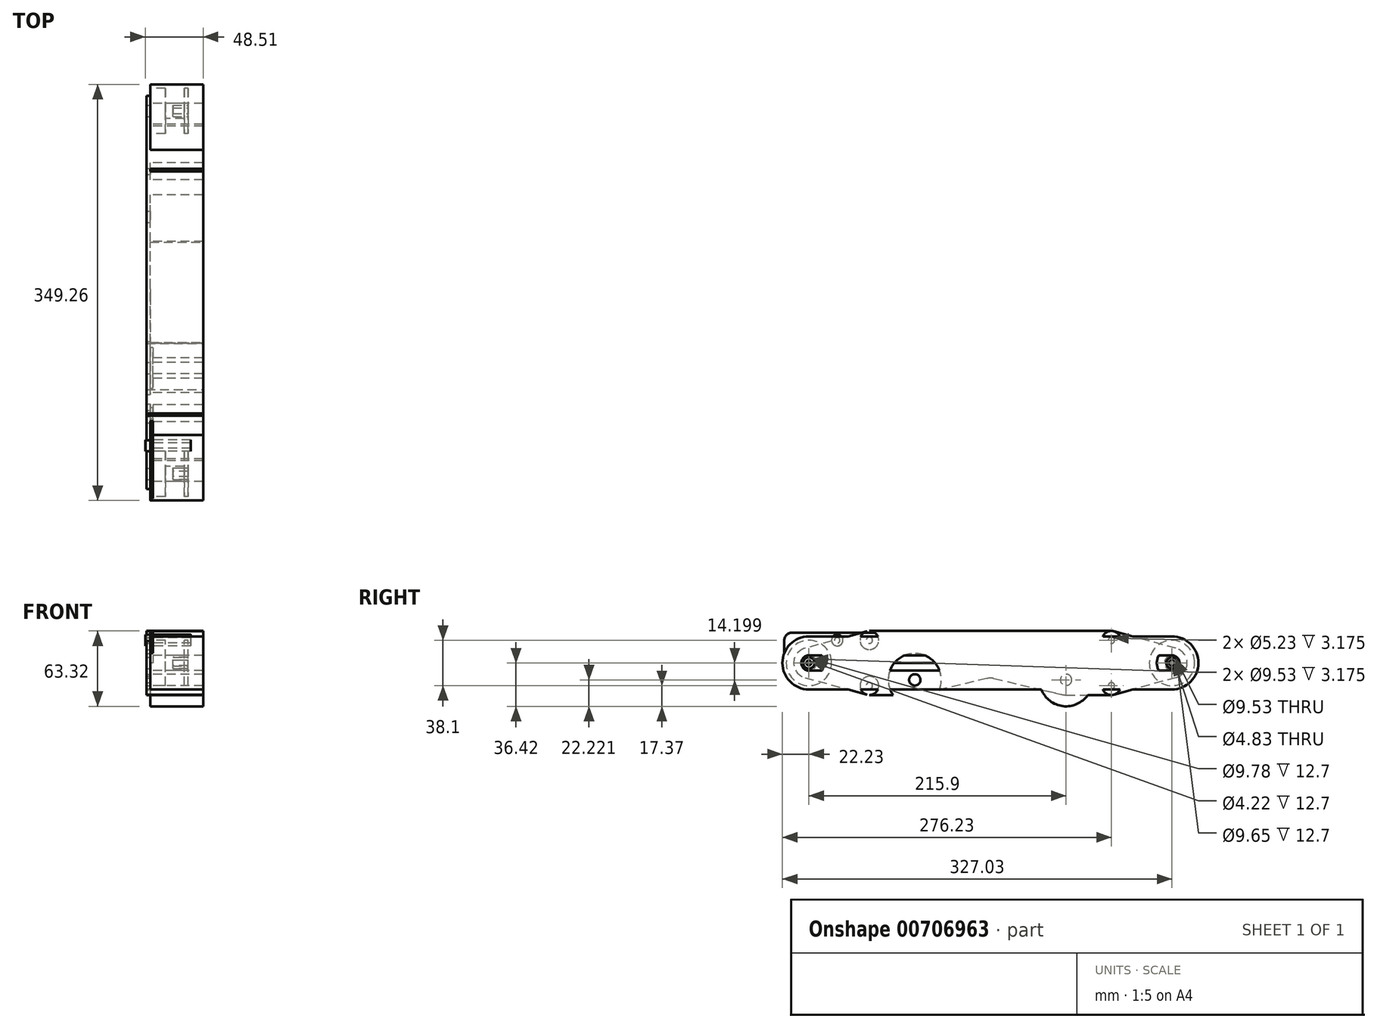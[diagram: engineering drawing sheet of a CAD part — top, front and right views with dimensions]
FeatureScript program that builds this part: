
annotation { "Feature Type Name" : "Feature", "Feature Type Description" : "" }
export const myFeature = defineFeature(function(context is Context, id is Id, definition is map)
    precondition{}
    {
        {
            var Q0;
            Q0=qCreatedBy(makeId("Right.planeOp"),FACE);
            var sketch = newSketch(context, id + "F0", { "sketchPlane" : qUnion([Q0])});
            skCircle(sketch, "E0", {"center": v(0, 0) * mm, "radius": 19.05 * mm});
            skCircle(sketch, "E1", {"center": v(304.8, 0) * mm, "radius": 19.05 * mm});
            skCircle(sketch, "E2", {"center": v(0, 0) * mm, "radius": 6.35 * mm});
            skCircle(sketch, "E3", {"center": v(304.8, 0) * mm, "radius": 6.35 * mm});
            skSolve(sketch);
        }
        {
            var Q0;
            Q0=makeQuery(id+"F0.imprint","IMPRINT",FACE,{"disambiguationData":[TD([[makeQuery(id+"F0.imprint","IMPRINT",EDGE,{"derivedFrom":sQuery(id+"F0.wireOp",EDGE,"E0")}),1.0]])]});
            var Q1;
            Q1=makeQuery(id+"F0.imprint","IMPRINT",FACE,{"disambiguationData":[TD([[makeQuery(id+"F0.imprint","IMPRINT",EDGE,{"derivedFrom":sQuery(id+"F0.wireOp",EDGE,"E1")}),1.0]])]});
            var Q2;
            Q2=makeQuery(id+"F0.imprint","IMPRINT",FACE,{"disambiguationData":[TD([[makeQuery(id+"F0.imprint","IMPRINT",EDGE,{"derivedFrom":sQuery(id+"F0.wireOp",EDGE,"E2")}),1.0]])]});
            var Q3;
            Q3=makeQuery(id+"F0.imprint","IMPRINT",FACE,{"disambiguationData":[TD([[makeQuery(id+"F0.imprint","IMPRINT",EDGE,{"derivedFrom":sQuery(id+"F0.wireOp",EDGE,"E3")}),1.0]])]});
            extrude(context, id + "F1", {"entities" : qUnion([Q0, Q1, Q2, Q3]), "depth" : 31.75 * mm, "offsetDistance" : 25.4 * mm});
        }
        {
            var Q0;
            Q0 = qSketchRegion(id + "F0", true);
            extrude(context, id + "F2", {"entities" : qUnion([Q0]), "operationType" : NewBodyOperationType.REMOVE, "depth" : 28.57 * mm, "offsetDistance" : 25.4 * mm, "hasSecondDirection" : true, "secondDirectionOppositeDirection" : true, "secondDirectionDepth" : -12.7 * mm});
        }
        {
            var Q0;
            Q0=qCreatedBy(makeId("Right.planeOp"),FACE);
            var sketch = newSketch(context, id + "F3", { "sketchPlane" : qUnion([Q0])});
            skCircle(sketch, "E4", {"center": v(0, 0) * mm, "radius": 12.7 * mm});
            skCircle(sketch, "E5", {"center": v(304.8, 0) * mm, "radius": 12.7 * mm});
            skLineSegment(sketch, "E6.bottom", {"start": v(25.4, 25.4) * mm, "end": v(279.4, 25.4) * mm, "construction": true});
            skLineSegment(sketch, "E6.top", {"start": v(25.4, -25.4) * mm, "end": v(279.4, -25.4) * mm, "construction": true});
            skLineSegment(sketch, "E6.left", {"start": v(25.4, 25.4) * mm, "end": v(25.4, -25.4) * mm, "construction": true});
            skLineSegment(sketch, "E6.right", {"start": v(279.4, 25.4) * mm, "end": v(279.4, -25.4) * mm, "construction": true});
            skLineSegment(sketch, "E7", {"start": v(25.4, 25.4) * mm, "end": v(-5.23, 11.58) * mm, "construction": true});
            skLineSegment(sketch, "E8", {"start": v(25.4, -25.4) * mm, "end": v(-5.23, -11.58) * mm, "construction": true});
            skLineSegment(sketch, "E9", {"start": v(279.4, 25.4) * mm, "end": v(310.03, 11.58) * mm, "construction": true});
            skLineSegment(sketch, "E10", {"start": v(279.4, -25.4) * mm, "end": v(310.03, -11.58) * mm, "construction": true});
            skCircle(sketch, "E11", {"center": v(0, 0) * mm, "radius": 4.76 * mm});
            skCircle(sketch, "E12", {"center": v(304.8, 0) * mm, "radius": 4.76 * mm});
            skCircle(sketch, "E13", {"center": v(215.9, -14.2) * mm, "radius": 4.76 * mm});
            skCircle(sketch, "E14", {"center": v(215.9, -14.2) * mm, "radius": 22.23 * mm});
            skCircle(sketch, "E15.0", {"center": v(304.8, 0) * mm, "radius": 19.05 * mm, "construction": true});
            skCircle(sketch, "E16.0", {"center": v(0, 0) * mm, "radius": 19.05 * mm, "construction": true});
            skLineSegment(sketch, "E17", {"start": v(152.4, 25.4) * mm, "end": v(152.4, -25.4) * mm, "construction": true});
            skCircle(sketch, "E18.MirrorC", {"center": v(88.9, -14.2) * mm, "radius": 22.23 * mm});
            skCircle(sketch, "E19.MirrorC", {"center": v(88.9, -14.2) * mm, "radius": 4.76 * mm});
            skCircle(sketch, "E20", {"center": v(215.9, -14.2) * mm, "radius": 12.7 * mm});
            skCircle(sketch, "E21.MirrorC", {"center": v(88.9, -14.2) * mm, "radius": 12.7 * mm});
            skCircle(sketch, "E22", {"center": v(254, 19.05) * mm, "radius": 2.62 * mm});
            skCircle(sketch, "E23", {"center": v(254, -19.05) * mm, "radius": 2.62 * mm});
            skLineSegment(sketch, "E24", {"start": v(254, 19.05) * mm, "end": v(254, -19.05) * mm, "construction": true});
            skCircle(sketch, "E25.MirrorC", {"center": v(50.8, -19.05) * mm, "radius": 2.62 * mm});
            skCircle(sketch, "E26.MirrorC", {"center": v(50.8, 19.05) * mm, "radius": 2.62 * mm});
            skCircle(sketch, "E27", {"center": v(254, 19.05) * mm, "radius": 7.85 * mm});
            skCircle(sketch, "E28", {"center": v(254, -19.05) * mm, "radius": 7.85 * mm});
            skLineSegment(sketch, "E29", {"start": v(304.8, 0) * mm, "end": v(0, 0) * mm, "construction": true});
            skCircle(sketch, "E30.MirrorC", {"center": v(50.8, -19.05) * mm, "radius": 7.85 * mm});
            skCircle(sketch, "E31.MirrorC", {"center": v(50.8, 19.05) * mm, "radius": 7.85 * mm});
            skLineSegment(sketch, "E32", {"start": v(48.71, 26.62) * mm, "end": v(-3.38, 12.24) * mm});
            skLineSegment(sketch, "E33", {"start": v(254, 26.9) * mm, "end": v(50.8, 26.9) * mm});
            skLineSegment(sketch, "E34", {"start": v(308.18, 12.24) * mm, "end": v(256.09, 26.62) * mm});
            skLineSegment(sketch, "E35", {"start": v(308.18, -12.24) * mm, "end": v(256.09, -26.62) * mm});
            skLineSegment(sketch, "E36", {"start": v(215.9, -26.9) * mm, "end": v(254, -26.9) * mm});
            skLineSegment(sketch, "E37", {"start": v(88.9, -26.9) * mm, "end": v(50.8, -26.9) * mm});
            skLineSegment(sketch, "E38", {"start": v(-3.38, -12.24) * mm, "end": v(48.71, -26.62) * mm});
            skLineSegment(sketch, "E39", {"start": v(215.9, -14.2) * mm, "end": v(88.9, -14.2) * mm, "construction": true});
            skCircle(sketch, "E40", {"center": v(152.4, -25.4) * mm, "radius": 12.7 * mm, "construction": true});
            skLineSegment(sketch, "E41", {"start": v(155.3, -13.04) * mm, "end": v(213, -26.56) * mm});
            skLineSegment(sketch, "E42", {"start": v(149.5, -13.04) * mm, "end": v(91.8, -26.56) * mm});
            skArc(sketch, "E43", {"start": v(155.3, -13.04) * mm, "mid": v(152.4, -12.7) * mm, "end": v(149.5, -13.04) * mm});
            skSolve(sketch);
        }
        {
            var Q0;
            Q0=makeQuery(id+"F3.imprint","IMPRINT",FACE,{"disambiguationData":[TD([[makeQuery(id+"F3.imprint","IMPRINT",EDGE,{"derivedFrom":sQuery(id+"F3.wireOp",EDGE,"E11")}),-1.0]])]});
            var Q1;
            Q1=makeQuery(id+"F3.imprint","IMPRINT",FACE,{"disambiguationData":[TD([[makeQuery(id+"F3.imprint","IMPRINT",EDGE,{"derivedFrom":sQuery(id+"F3.wireOp",EDGE,"E6.left")}),-1.0]])]});
            var Q2;
            Q2=makeQuery(id+"F3.imprint","IMPRINT",FACE,{"disambiguationData":[TD([[makeQuery(id+"F3.imprint","IMPRINT",EDGE,{"derivedFrom":sQuery(id+"F3.wireOp",EDGE,"E6.bottom")}),-1.0]])]});
            var Q3;
            Q3=makeQuery(id+"F3.imprint","IMPRINT",FACE,{"disambiguationData":[TD([[makeQuery(id+"F3.imprint","IMPRINT",EDGE,{"derivedFrom":sQuery(id+"F3.wireOp",EDGE,"E12")}),-1.0]])]});
            var Q4;
            Q4=makeQuery(id+"F3.imprint","IMPRINT",FACE,{"disambiguationData":[TD([[makeQuery(id+"F3.imprint","IMPRINT",EDGE,{"derivedFrom":sQuery(id+"F3.wireOp",EDGE,"E6.right")}),1.0]])]});
            var Q5;
            {var subQ1=sQuery(id+"F3.wireOp",EDGE,"E32");Q5=makeQuery(id+"F3.imprint","IMPRINT",FACE,{"disambiguationData":[TD([[makeQuery(id+"F3.imprint","IMPRINT",EDGE,{"derivedFrom":subQ1}),1.0]])]});}
            var Q6;
            Q6=makeQuery(id+"F3.imprint","IMPRINT",FACE,{"disambiguationData":[TD([[makeQuery(id+"F3.imprint","IMPRINT",EDGE,{"derivedFrom":sQuery(id+"F3.wireOp",EDGE,"E26.MirrorC")}),1.0]])]});
            var Q7;
            Q7=makeQuery(id+"F3.imprint","IMPRINT",FACE,{"disambiguationData":[TD([[makeQuery(id+"F3.imprint","IMPRINT",EDGE,{"derivedFrom":sQuery(id+"F3.wireOp",EDGE,"E25.MirrorC")}),1.0]])]});
            var Q8;
            Q8=makeQuery(id+"F3.imprint","IMPRINT",FACE,{"disambiguationData":[TD([[makeQuery(id+"F3.imprint","IMPRINT",EDGE,{"derivedFrom":sQuery(id+"F3.wireOp",EDGE,"E19.MirrorC")}),1.0]])]});
            var Q9;
            {var subQ0=sQuery(id+"F3.wireOp",EDGE,"E37");var subQ1=sQuery(id+"F3.wireOp",EDGE,"E18.MirrorC");var subQ2=makeQuery(id+"F3.imprint","INTERSECT",VERTEX,{"derivedFrom":[subQ1,subQ0]});Q9=makeQuery(id+"F3.imprint","IMPRINT",FACE,{"disambiguationData":[TD([[makeQuery(id+"F3.imprint","IMPRINT",EDGE,{"disambiguationData":[TD([[subQ2,-1.0]])],"derivedFrom":subQ1}),-1.0]])]});}
            var Q10;
            Q10=makeQuery(id+"F3.imprint","IMPRINT",FACE,{"disambiguationData":[TD([[makeQuery(id+"F3.imprint","IMPRINT",EDGE,{"derivedFrom":sQuery(id+"F3.wireOp",EDGE,"E23")}),-1.0]])]});
            var Q11;
            Q11=makeQuery(id+"F3.imprint","IMPRINT",FACE,{"disambiguationData":[TD([[makeQuery(id+"F3.imprint","IMPRINT",EDGE,{"derivedFrom":sQuery(id+"F3.wireOp",EDGE,"E22")}),-1.0]])]});
            var Q12;
            Q12=makeQuery(id+"F3.imprint","IMPRINT",FACE,{"disambiguationData":[TD([[makeQuery(id+"F3.imprint","IMPRINT",EDGE,{"derivedFrom":sQuery(id+"F3.wireOp",EDGE,"E13")}),-1.0]])]});
            var Q13;
            {var subQ0=sQuery(id+"F3.wireOp",EDGE,"E36");var subQ1=sQuery(id+"F3.wireOp",EDGE,"E14");var subQ2=makeQuery(id+"F3.imprint","INTERSECT",VERTEX,{"derivedFrom":[subQ1,subQ0]});Q13=makeQuery(id+"F3.imprint","IMPRINT",FACE,{"disambiguationData":[TD([[makeQuery(id+"F3.imprint","IMPRINT",EDGE,{"disambiguationData":[TD([[subQ2,-1.0]])],"derivedFrom":subQ1}),1.0]])]});}
            extrude(context, id + "F4", {"entities" : qUnion([Q0, Q1, Q2, Q3, Q4, Q5, Q6, Q7, Q8, Q9, Q10, Q11, Q12, Q13]), "oppositeDirection" : true, "depth" : 3.17 * mm, "offsetDistance" : 25.4 * mm});
        }
        {
            var Q0;
            {var subQ0=sQuery(id+"F3.wireOp",EDGE,"E37");var subQ1=sQuery(id+"F3.wireOp",EDGE,"E18.MirrorC");var subQ2=makeQuery(id+"F3.imprint","INTERSECT",VERTEX,{"derivedFrom":[subQ1,subQ0]});Q0=makeQuery(id+"F3.imprint","IMPRINT",FACE,{"disambiguationData":[TD([[makeQuery(id+"F3.imprint","IMPRINT",EDGE,{"disambiguationData":[TD([[subQ2,1.0]])],"derivedFrom":subQ1}),-1.0]])]});}
            var Q1;
            {var subQ0=sQuery(id+"F3.wireOp",EDGE,"E37");var subQ1=sQuery(id+"F3.wireOp",EDGE,"E18.MirrorC");var subQ2=makeQuery(id+"F3.imprint","INTERSECT",VERTEX,{"derivedFrom":[subQ1,subQ0]});Q1=makeQuery(id+"F3.imprint","IMPRINT",FACE,{"disambiguationData":[TD([[makeQuery(id+"F3.imprint","IMPRINT",EDGE,{"disambiguationData":[TD([[subQ2,-1.0]])],"derivedFrom":subQ1}),-1.0]])]});}
            var Q2;
            Q2=makeQuery(id+"F3.imprint","IMPRINT",FACE,{"disambiguationData":[TD([[makeQuery(id+"F3.imprint","IMPRINT",EDGE,{"derivedFrom":sQuery(id+"F3.wireOp",EDGE,"E19.MirrorC")}),1.0]])]});
            var Q3;
            {var subQ0=sQuery(id+"F3.wireOp",EDGE,"E36");var subQ1=sQuery(id+"F3.wireOp",EDGE,"E14");var subQ2=makeQuery(id+"F3.imprint","INTERSECT",VERTEX,{"derivedFrom":[subQ1,subQ0]});Q3=makeQuery(id+"F3.imprint","IMPRINT",FACE,{"disambiguationData":[TD([[makeQuery(id+"F3.imprint","IMPRINT",EDGE,{"disambiguationData":[TD([[subQ2,-1.0]])],"derivedFrom":subQ1}),1.0]])]});}
            var Q4;
            Q4=makeQuery(id+"F3.imprint","IMPRINT",FACE,{"disambiguationData":[TD([[makeQuery(id+"F3.imprint","IMPRINT",EDGE,{"derivedFrom":sQuery(id+"F3.wireOp",EDGE,"E13")}),-1.0]])]});
            var Q5;
            {var subQ0=sQuery(id+"F3.wireOp",EDGE,"E36");var subQ1=sQuery(id+"F3.wireOp",EDGE,"E14");var subQ2=makeQuery(id+"F3.imprint","INTERSECT",VERTEX,{"derivedFrom":[subQ1,subQ0]});Q5=makeQuery(id+"F3.imprint","IMPRINT",FACE,{"disambiguationData":[TD([[makeQuery(id+"F3.imprint","IMPRINT",EDGE,{"disambiguationData":[TD([[subQ2,1.0]])],"derivedFrom":subQ1}),1.0]])]});}
            extrude(context, id + "F5", {"entities" : qUnion([Q0, Q1, Q2, Q3, Q4, Q5]), "depth" : 44.45 * mm, "offsetDistance" : 25.4 * mm});
        }
        {
            var Q0;
            Q0=qCreatedBy(makeId("Right.planeOp"),FACE);
            var sketch = newSketch(context, id + "F6", { "sketchPlane" : qUnion([Q0])});
            skCircle(sketch, "E44.0", {"center": v(0, 0) * mm, "radius": 6.35 * mm});
            skCircle(sketch, "E45.0", {"center": v(304.8, 0) * mm, "radius": 6.35 * mm});
            skCircle(sketch, "E46", {"center": v(0, 0) * mm, "radius": 22.23 * mm});
            skCircle(sketch, "E47.0", {"center": v(0, 0) * mm, "radius": 19.05 * mm, "construction": true});
            skCircle(sketch, "E48.0", {"center": v(304.8, 0) * mm, "radius": 19.05 * mm, "construction": true});
            skCircle(sketch, "E49", {"center": v(304.8, 0) * mm, "radius": 22.23 * mm});
            skLineSegment(sketch, "E50", {"start": v(0, 6.35) * mm, "end": v(304.8, 6.35) * mm});
            skLineSegment(sketch, "E51", {"start": v(304.8, 22.23) * mm, "end": v(0, 22.23) * mm});
            skLineSegment(sketch, "E52", {"start": v(0, -6.35) * mm, "end": v(304.8, -6.35) * mm});
            skLineSegment(sketch, "E53", {"start": v(0, -22.23) * mm, "end": v(304.8, -22.22) * mm});
            skSolve(sketch);
        }
        {
            var Q0;
            {var subQ0=sQuery(id+"F6.wireOp",EDGE,"E51");Q0=makeQuery(id+"F6.imprint","IMPRINT",FACE,{"disambiguationData":[TD([[makeQuery(id+"F6.imprint","IMPRINT",EDGE,{"derivedFrom":subQ0}),1.0]])]});}
            var Q1;
            {var subQ5=sQuery(id+"F6.wireOp",EDGE,"E50");var subQ7=sQuery(id+"F6.wireOp",EDGE,"E44.0");var subQ9=makeQuery(id+"F6.imprint","INTERSECT",VERTEX,{"derivedFrom":[subQ7,subQ5]});Q1=makeQuery(id+"F6.imprint","IMPRINT",FACE,{"disambiguationData":[TD([[makeQuery(id+"F6.imprint","IMPRINT",EDGE,{"disambiguationData":[TD([[subQ9,-1.0]])],"derivedFrom":subQ7}),-1.0]])]});}
            var Q2;
            {var subQ0=sQuery(id+"F6.wireOp",EDGE,"E53");Q2=makeQuery(id+"F6.imprint","IMPRINT",FACE,{"disambiguationData":[TD([[makeQuery(id+"F6.imprint","IMPRINT",EDGE,{"derivedFrom":subQ0}),1.0]])]});}
            var Q3;
            {var subQ5=sQuery(id+"F6.wireOp",EDGE,"E50");var subQ7=sQuery(id+"F6.wireOp",EDGE,"E45.0");var subQ8=makeQuery(id+"F6.imprint","INTERSECT",VERTEX,{"derivedFrom":[subQ7,subQ5]});Q3=makeQuery(id+"F6.imprint","IMPRINT",FACE,{"disambiguationData":[TD([[makeQuery(id+"F6.imprint","IMPRINT",EDGE,{"disambiguationData":[TD([[subQ8,1.0]])],"derivedFrom":subQ7}),-1.0]])]});}
            extrude(context, id + "F7", {"entities" : qUnion([Q0, Q1, Q2, Q3]), "depth" : 44.45 * mm, "offsetDistance" : 25.4 * mm});
        }
        {
            var Q0;
            Q0=qCreatedBy(makeId("Right.planeOp"),FACE);
            var sketch = newSketch(context, id + "F8", { "sketchPlane" : qUnion([Q0])});
            skLineSegment(sketch, "E54.bottom", {"start": v(-14.29, 25.4) * mm, "end": v(227.01, 25.4) * mm});
            skLineSegment(sketch, "E54.top", {"start": v(-14.29, 0) * mm, "end": v(227.01, 0) * mm});
            skLineSegment(sketch, "E54.left", {"start": v(-20.64, 19.05) * mm, "end": v(-20.64, 6.35) * mm});
            skLineSegment(sketch, "E54.right", {"start": v(233.36, 19.05) * mm, "end": v(233.36, 6.35) * mm});
            skPoint(sketch, "E55.visualSharp", {"position": v(-20.64, 25.4) * mm});
            skArc(sketch, "E55.filletArc", {"start": v(-14.29, 25.4) * mm, "mid": v(-18.78, 23.54) * mm, "end": v(-20.64, 19.05) * mm});
            skPoint(sketch, "E56.visualSharp", {"position": v(-20.64, 0) * mm});
            skArc(sketch, "E56.filletArc", {"start": v(-20.64, 6.35) * mm, "mid": v(-18.78, 1.86) * mm, "end": v(-14.29, 0) * mm});
            skPoint(sketch, "E57.visualSharp", {"position": v(233.36, 0) * mm});
            skArc(sketch, "E57.filletArc", {"start": v(227.01, 0) * mm, "mid": v(231.5, 1.86) * mm, "end": v(233.36, 6.35) * mm});
            skPoint(sketch, "E58.visualSharp", {"position": v(233.36, 25.4) * mm});
            skArc(sketch, "E58.filletArc", {"start": v(233.36, 19.05) * mm, "mid": v(231.5, 23.54) * mm, "end": v(227.01, 25.4) * mm});
            skCircle(sketch, "E59", {"center": v(-7.94, 12.7) * mm, "radius": 4.76 * mm});
            skCircle(sketch, "E60", {"center": v(0, 12.7) * mm, "radius": 2.03 * mm});
            skCircle(sketch, "E61", {"center": v(-15.88, 12.7) * mm, "radius": 2.03 * mm});
            skLineSegment(sketch, "E62", {"start": v(-15.88, 12.7) * mm, "end": v(0, 12.7) * mm, "construction": true});
            skLineSegment(sketch, "E63", {"start": v(0, 12.7) * mm, "end": v(220.66, 12.7) * mm, "construction": true});
            skCircle(sketch, "E64", {"center": v(55.56, 12.7) * mm, "radius": 2.29 * mm});
            skCircle(sketch, "E65", {"center": v(157.16, 12.7) * mm, "radius": 2.29 * mm});
            skCircle(sketch, "E66", {"center": v(220.66, 12.7) * mm, "radius": 2.29 * mm});
            skCircle(sketch, "E67", {"center": v(23.81, 19.05) * mm, "radius": 2.29 * mm});
            skCircle(sketch, "E68", {"center": v(23.81, 6.35) * mm, "radius": 2.29 * mm});
            skCircle(sketch, "E69", {"center": v(188.91, 19.05) * mm, "radius": 2.29 * mm});
            skCircle(sketch, "E70", {"center": v(188.91, 6.35) * mm, "radius": 2.29 * mm});
            skLineSegment(sketch, "E71", {"start": v(23.81, 19.05) * mm, "end": v(188.91, 19.05) * mm, "construction": true});
            skLineSegment(sketch, "E72", {"start": v(188.91, 6.35) * mm, "end": v(23.81, 6.35) * mm, "construction": true});
            skLineSegment(sketch, "E73", {"start": v(106.36, 25.4) * mm, "end": v(106.36, 0) * mm, "construction": true});
            skLineSegment(sketch, "E74", {"start": v(188.91, 19.05) * mm, "end": v(188.91, 6.35) * mm, "construction": true});
            skLineSegment(sketch, "E75", {"start": v(23.81, 19.05) * mm, "end": v(23.81, 6.35) * mm, "construction": true});
            skCircle(sketch, "E76", {"center": v(106.36, 19.05) * mm, "radius": 2.29 * mm});
            skCircle(sketch, "E77", {"center": v(106.36, 6.35) * mm, "radius": 2.29 * mm});
            skSolve(sketch);
        }
        {
            var Q0;
            Q0=makeQuery(id+"F8.imprint","IMPRINT",FACE,{"disambiguationData":[TD([[makeQuery(id+"F8.imprint","IMPRINT",EDGE,{"derivedFrom":sQuery(id+"F8.wireOp",EDGE,"E54.bottom")}),-1.0]])]});
            extrude(context, id + "F9", {"entities" : qUnion([Q0]), "depth" : 2.3 * mm, "offsetDistance" : 25.4 * mm});
        }
        {
            var Q0;
            Q0=makeQuery(id+"F9.opExtrude","CAP_FACE",FACE,{"disambiguationData":[OSD([sQuery(id+"F8.wireOp",EDGE,"E54.bottom"),sQuery(id+"F8.wireOp",EDGE,"E54.top"),sQuery(id+"F8.wireOp",EDGE,"E54.left"),sQuery(id+"F8.wireOp",EDGE,"E54.right"),sQuery(id+"F8.wireOp",EDGE,"E55.filletArc"),sQuery(id+"F8.wireOp",EDGE,"E56.filletArc"),sQuery(id+"F8.wireOp",EDGE,"E57.filletArc"),sQuery(id+"F8.wireOp",EDGE,"E58.filletArc"),sQuery(id+"F8.wireOp",EDGE,"E59"),sQuery(id+"F8.wireOp",EDGE,"E60"),sQuery(id+"F8.wireOp",EDGE,"E61"),sQuery(id+"F8.wireOp",EDGE,"E64"),sQuery(id+"F8.wireOp",EDGE,"E65"),sQuery(id+"F8.wireOp",EDGE,"E66"),sQuery(id+"F8.wireOp",EDGE,"E67"),sQuery(id+"F8.wireOp",EDGE,"E68"),sQuery(id+"F8.wireOp",EDGE,"E69"),sQuery(id+"F8.wireOp",EDGE,"E70"),sQuery(id+"F8.wireOp",EDGE,"E76"),sQuery(id+"F8.wireOp",EDGE,"E77")])],"isStart":false});
            var sketch = newSketch(context, id + "F10", { "sketchPlane" : qUnion([Q0])});
            skCircle(sketch, "E78.0", {"center": v(23.81, 19.05) * mm, "radius": 2.29 * mm});
            skCircle(sketch, "E79", {"center": v(23.81, 19.05) * mm, "radius": 4.76 * mm});
            skCircle(sketch, "E80", {"center": v(23.81, 19.05) * mm, "radius": 2.03 * mm});
            skSolve(sketch);
        }
        {
            var Q0;
            Q0=makeQuery(id+"F10.imprint","IMPRINT",FACE,{"disambiguationData":[TD([[makeQuery(id+"F10.imprint","IMPRINT",EDGE,{"derivedFrom":sQuery(id+"F10.wireOp",EDGE,"E78.0")}),-1.0]])]});
            extrude(context, id + "F11", {"entities" : qUnion([Q0]), "depth" : 31.75 * mm, "offsetDistance" : 25.4 * mm});
        }
        {
            var Q0;
            Q0=makeQuery(id+"F10.imprint","IMPRINT",FACE,{"disambiguationData":[TD([[makeQuery(id+"F10.imprint","IMPRINT",EDGE,{"derivedFrom":sQuery(id+"F10.wireOp",EDGE,"E80")}),1.0]])]});
            extrude(context, id + "F12", {"entities" : qUnion([Q0]), "depth" : 38.1 * mm, "offsetDistance" : 25.4 * mm, "hasSecondDirection" : true, "secondDirectionOppositeDirection" : true, "secondDirectionDepth" : 2.3 * mm});
        }
        {
            var Q0;
            Q0=makeQuery(id+"F10.imprint","IMPRINT",FACE,{"disambiguationData":[TD([[makeQuery(id+"F10.imprint","IMPRINT",EDGE,{"derivedFrom":sQuery(id+"F10.wireOp",EDGE,"E78.0")}),-1.0]])]});
            var Q1;
            Q1=makeQuery(id+"F10.imprint","IMPRINT",FACE,{"disambiguationData":[TD([[makeQuery(id+"F10.imprint","IMPRINT",EDGE,{"derivedFrom":sQuery(id+"F10.wireOp",EDGE,"E78.0")}),1.0]])]});
            var Q2;
            Q2=makeQuery(id+"F10.imprint","IMPRINT",FACE,{"disambiguationData":[TD([[makeQuery(id+"F10.imprint","IMPRINT",EDGE,{"derivedFrom":sQuery(id+"F10.wireOp",EDGE,"E80")}),1.0]])]});
            extrude(context, id + "F13", {"entities" : qUnion([Q0, Q1, Q2]), "operationType" : NewBodyOperationType.ADD, "oppositeDirection" : true, "depth" : 6.35 * mm, "offsetDistance" : 25.4 * mm, "hasSecondDirection" : true, "secondDirectionOppositeDirection" : false, "secondDirectionDepth" : -2.3 * mm});
        }
        {
            var Q0;
            Q0=makeQuery(id+"F1.opExtrude","CAP_FACE",FACE,{"disambiguationData":[OSD([sQuery(id+"F0.wireOp",EDGE,"E0")])],"isStart":false});
            var sketch = newSketch(context, id + "F14", { "sketchPlane" : qUnion([Q0])});
            skCircle(sketch, "E81.0", {"center": v(0, 0) * mm, "radius": 19.05 * mm});
            skCircle(sketch, "E82", {"center": v(0, 0) * mm, "radius": 4.89 * mm});
            skSolve(sketch);
        }
        {
            var Q0;
            Q0=makeQuery(id+"F14.imprint","IMPRINT",FACE,{"disambiguationData":[TD([[makeQuery(id+"F14.imprint","IMPRINT",EDGE,{"derivedFrom":sQuery(id+"F14.wireOp",EDGE,"E82")}),1.0]])]});
            extrude(context, id + "F15", {"entities" : qUnion([Q0]), "operationType" : NewBodyOperationType.REMOVE, "oppositeDirection" : true, "depth" : 12.7 * mm, "offsetDistance" : 25.4 * mm});
        }
        {
            var Q0;
            Q0=makeQuery(id+"F15.boolean.opBoolean","COPY",FACE,{"derivedFrom":makeQuery(id+"F15.opExtrude","CAP_FACE",FACE,{"disambiguationData":[OSD([sQuery(id+"F14.wireOp",EDGE,"E82")])],"isStart":false})});
            var sketch = newSketch(context, id + "F16", { "sketchPlane" : qUnion([Q0])});
            skCircle(sketch, "E83.0", {"center": v(0, 0) * mm, "radius": 4.89 * mm});
            skCircle(sketch, "E84", {"center": v(0, 0) * mm, "radius": 4.76 * mm});
            skCircle(sketch, "E85", {"center": v(0, 0) * mm, "radius": 2.1 * mm});
            skSolve(sketch);
        }
        {
            var Q0;
            Q0=makeQuery(id+"F16.imprint","IMPRINT",FACE,{"disambiguationData":[TD([[makeQuery(id+"F16.imprint","IMPRINT",EDGE,{"derivedFrom":sQuery(id+"F16.wireOp",EDGE,"E84")}),1.0]])]});
            extrude(context, id + "F17", {"entities" : qUnion([Q0]), "operationType" : NewBodyOperationType.ADD, "depth" : 12.7 * mm, "offsetDistance" : 25.4 * mm});
        }
        {
            var Q0;
            Q0=makeQuery(id+"F1.opExtrude","CAP_FACE",FACE,{"disambiguationData":[OSD([sQuery(id+"F0.wireOp",EDGE,"E1")])],"isStart":false});
            var sketch = newSketch(context, id + "F18", { "sketchPlane" : qUnion([Q0])});
            skCircle(sketch, "E86.0", {"center": v(304.8, 0) * mm, "radius": 19.05 * mm});
            skCircle(sketch, "E87", {"center": v(304.8, 0) * mm, "radius": 4.83 * mm});
            skCircle(sketch, "E88", {"center": v(304.8, 0) * mm, "radius": 4.7 * mm});
            skCircle(sketch, "E89", {"center": v(304.8, 0) * mm, "radius": 2.41 * mm});
            skSolve(sketch);
        }
        {
            var Q0;
            Q0=makeQuery(id+"F18.imprint","IMPRINT",FACE,{"disambiguationData":[TD([[makeQuery(id+"F18.imprint","IMPRINT",EDGE,{"derivedFrom":sQuery(id+"F18.wireOp",EDGE,"E87")}),1.0]])]});
            var Q1;
            Q1=makeQuery(id+"F18.imprint","IMPRINT",FACE,{"disambiguationData":[TD([[makeQuery(id+"F18.imprint","IMPRINT",EDGE,{"derivedFrom":sQuery(id+"F18.wireOp",EDGE,"E88")}),1.0]])]});
            var Q2;
            Q2=makeQuery(id+"F18.imprint","IMPRINT",FACE,{"disambiguationData":[TD([[makeQuery(id+"F18.imprint","IMPRINT",EDGE,{"derivedFrom":sQuery(id+"F18.wireOp",EDGE,"E89")}),1.0]])]});
            extrude(context, id + "F19", {"entities" : qUnion([Q0, Q1, Q2]), "operationType" : NewBodyOperationType.REMOVE, "oppositeDirection" : true, "depth" : 12.7 * mm, "offsetDistance" : 25.4 * mm});
        }
        {
            var Q0;
            Q0=makeQuery(id+"F18.imprint","IMPRINT",FACE,{"disambiguationData":[TD([[makeQuery(id+"F18.imprint","IMPRINT",EDGE,{"derivedFrom":sQuery(id+"F18.wireOp",EDGE,"E88")}),1.0]])]});
            extrude(context, id + "F20", {"entities" : qUnion([Q0]), "oppositeDirection" : true, "depth" : 12.7 * mm, "offsetDistance" : 25.4 * mm});
        }
    });
